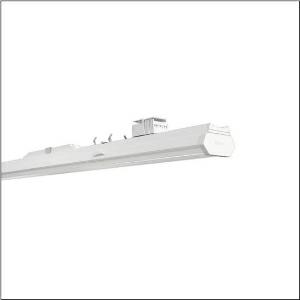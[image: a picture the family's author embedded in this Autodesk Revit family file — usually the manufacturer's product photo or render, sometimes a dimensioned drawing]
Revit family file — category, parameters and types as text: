
# Revit family: licross_r__11_protected_mo_51tp12dn495g3s_1208
name_source: partatom
category: Lighting Fixtures
units: mm (PartAtom-declared; Revit-internal decimal feet)

## family parameters
Cut with Voids When Loaded = No
Host = Face
Light Source = No
Part Type = Normal
Room Calculation Point = No
Round Connector Dimension = Use Diameter
Shared = No

## types (1)
- --- (1 x LED, 980 lm, 6.8 W, 4000K)
    Apparent Load = 7 VA
    CIE Flux Codes = 73 92 98 99 100
    Color Rendering = 80
    Color Temperature = 4000K
    Default Elevation = 1800 mm
    Description = Licross® 11 Protected MO, luminaire insert, of sheet steel, galvanised, coil coated, white, length: 1.500mm, width: 90mm, height: 101mm, LED rated luminous flux: 9.980lm, light colour: 840, control gear: DALI 2 (for two DALI lines), with plug, 6-pole, with phase selection, for trunking rail, 14-core, mains connection: 220..240V, AC, 50/60Hz, rated input power: 61W, for trunking rail, 14-core, halogen-free wiring, for emergency light function, converter,control gear: single battery element, battery: LiFePO4, 9Ah, primary light control with lens, of plastic, primary optical cover: cover, of PMMA, light emission: direct distribution, primary light characteristic: symmetric, protection rating (complete): IP64, insulation class (complete): insulation class I (protective earthing), certification: CE, UKCA, protection symbol: D if used in an environment with conductive dust loads with corresponding accessories, impact resistance: IK06, permissible ambient temperature for indoor applications: +5..+35°C, standard: EN 60598-2-22, LABS conformity tested according to VDMA 24364:2018-05, reducing of maximum allowable ambient temperature of 5°C with ceiling mounting, corresponds to IFS (International Featured Standards) requirements for safety and quality in the food industry, packaging unit: 1 piece
    Height = 92 mm
    Lamp = 1 x LED
    Lamp Light Flux = 980 lm
    Lamp Power = 6.8 W
    Lamp count = 1
    Length = 1500 mm
    Luminous efficacy = 144 lm/W
    Manufacturer = Siteco
    ModVariant = No
    Model = 51TP12DN495G3S
    Mounting Place = Ceiling
    Mounting Type = Pendant
    Number of Poles = 1
    OnlyDefault = Yes
    Power Factor = 1
    Product Name = Licross® 11 Protected MO
    Product group = luminaire insert
    ProductGroupID = 902
    Protection Class = Protection class I
    Protection Degree = IP 64
    RLX_Detail_Level = 1
    RLX_Emergency_Light_Flux = 0 lm
    RLX_Emergency_Type = 0
    RLX_Emergency_Type_DB = No
    RlxData = <blob elided: 24733 chars, md5=fb2dfb64>
    Socket = socket
    Standby Power = 0 W
    System Light Flux = 980 lm
    System Power = 7 W
    Type Comments = : emergency light operation: 3 h
    Type Image = l_1256148.jpg
    URL = http://relux.com
    VarID = @adj_090684
    Voltage = 0 V
    Weight = 0.00 kg
    Width = 88 mm

## geometry (parser evidence)
native form markers: Blend x4, Sweep x9
no freeform markers — native parametric forms only
